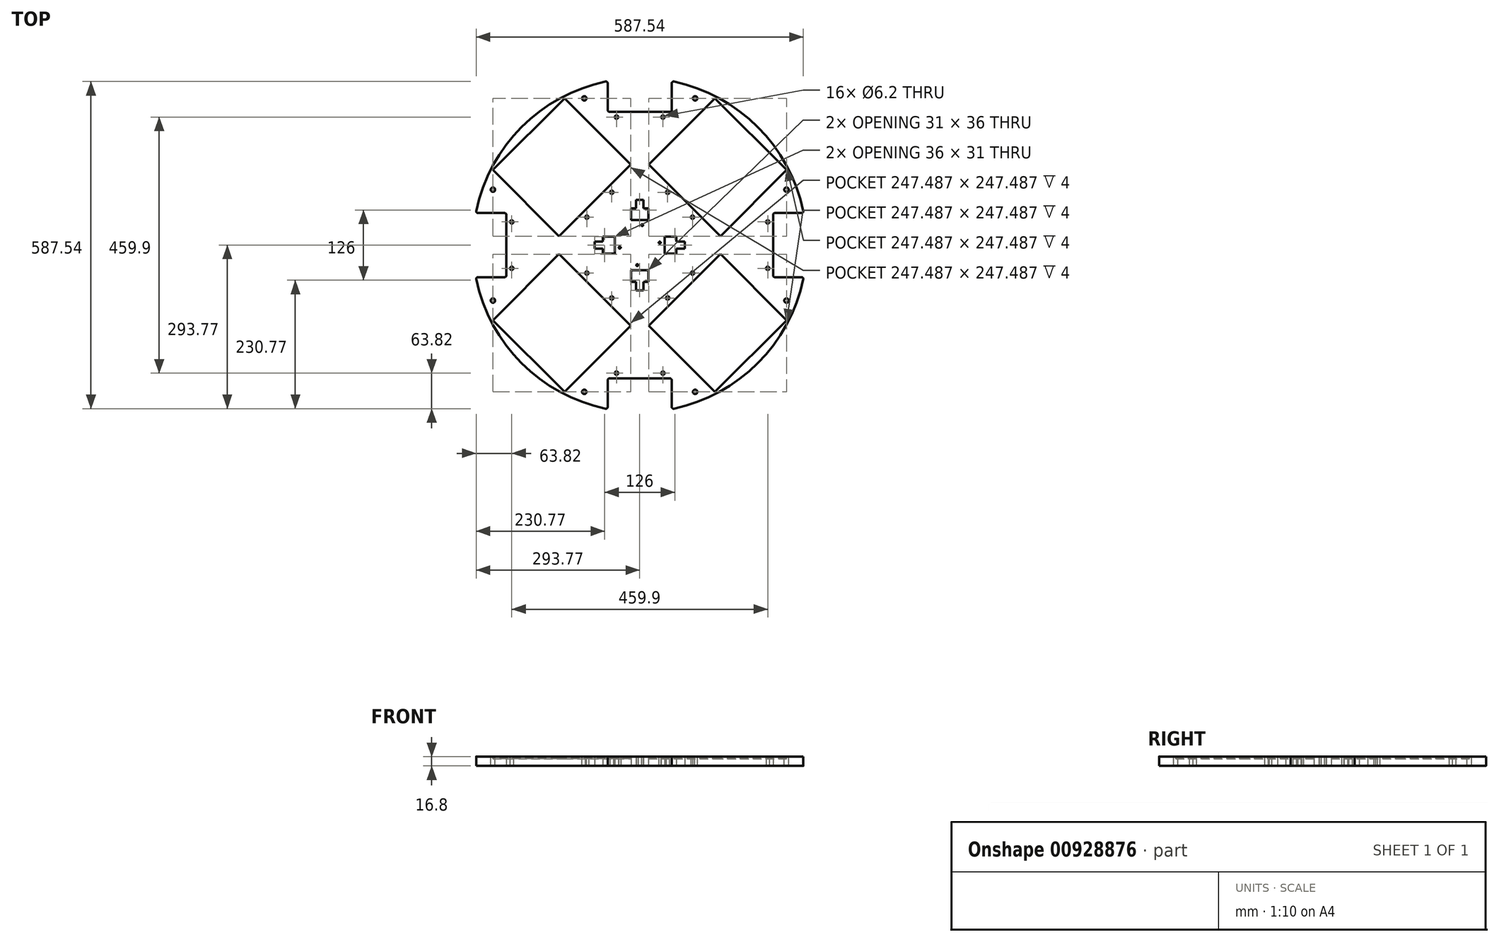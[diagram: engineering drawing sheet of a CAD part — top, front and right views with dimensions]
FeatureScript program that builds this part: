
annotation { "Feature Type Name" : "Feature", "Feature Type Description" : "" }
export const myFeature = defineFeature(function(context is Context, id is Id, definition is map)
    precondition{}
    {
        {
            var Q0;
            Q0=qCreatedBy(makeId("Top.planeOp"),FACE);
            var sketch = newSketch(context, id + "F0", { "sketchPlane" : qUnion([Q0])});
            skCircle(sketch, "E0", {"center": v(0, 0) * mm, "radius": 300 * mm});
            skLineSegment(sketch, "E1", {"start": v(300, 0) * mm, "end": v(-300, 0) * mm, "construction": true});
            skLineSegment(sketch, "E2", {"start": v(0, -300) * mm, "end": v(0, 300) * mm, "construction": true});
            skLineSegment(sketch, "E3.bottom", {"start": v(-296.52, 57.5) * mm, "end": v(-239.5, 57.5) * mm});
            skLineSegment(sketch, "E3.top", {"start": v(-296.52, -57.5) * mm, "end": v(-239.5, -57.5) * mm});
            skLineSegment(sketch, "E3.left", {"start": v(-296.52, 57.5) * mm, "end": v(-296.52, -57.5) * mm, "construction": true});
            skLineSegment(sketch, "E3.right", {"start": v(-239.5, 57.5) * mm, "end": v(-239.5, -57.5) * mm});
            skPoint(sketch, "E3.middle", {"position": v(-268, 0) * mm});
            skLineSegment(sketch, "E4.1.0", {"start": v(-57.5, -296.52) * mm, "end": v(-57.5, -239.5) * mm});
            skLineSegment(sketch, "E4.1.1", {"start": v(57.5, -296.52) * mm, "end": v(57.5, -239.5) * mm});
            skLineSegment(sketch, "E4.1.2", {"start": v(-57.5, -296.52) * mm, "end": v(57.5, -296.52) * mm});
            skLineSegment(sketch, "E4.1.3", {"start": v(-57.5, -239.5) * mm, "end": v(57.5, -239.5) * mm});
            skPoint(sketch, "E4.1.4", {"position": v(0, -268) * mm});
            skLineSegment(sketch, "E4.2.0", {"start": v(296.52, -57.5) * mm, "end": v(239.5, -57.5) * mm});
            skLineSegment(sketch, "E4.2.1", {"start": v(296.52, 57.5) * mm, "end": v(239.5, 57.5) * mm});
            skLineSegment(sketch, "E4.2.2", {"start": v(296.52, -57.5) * mm, "end": v(296.52, 57.5) * mm});
            skLineSegment(sketch, "E4.2.3", {"start": v(239.5, -57.5) * mm, "end": v(239.5, 57.5) * mm});
            skPoint(sketch, "E4.2.4", {"position": v(268, 0) * mm});
            skLineSegment(sketch, "E4.3.0", {"start": v(57.5, 296.52) * mm, "end": v(57.5, 239.5) * mm});
            skLineSegment(sketch, "E4.3.1", {"start": v(-57.5, 296.52) * mm, "end": v(-57.5, 239.5) * mm});
            skLineSegment(sketch, "E4.3.2", {"start": v(57.5, 296.52) * mm, "end": v(-57.5, 296.52) * mm});
            skLineSegment(sketch, "E4.3.3", {"start": v(57.5, 239.5) * mm, "end": v(-57.5, 239.5) * mm});
            skPoint(sketch, "E4.3.4", {"position": v(0, 268) * mm});
            skLineSegment(sketch, "E5", {"start": v(-239.5, -57.5) * mm, "end": v(-94.95, -57.5) * mm, "construction": true});
            skLineSegment(sketch, "E6", {"start": v(-229.95, -41.7) * mm, "end": v(-229.95, 0) * mm, "construction": true});
            skCircle(sketch, "E7", {"center": v(-229.95, -41.7) * mm, "radius": 3.1 * mm});
            skCircle(sketch, "E8.MirrorC", {"center": v(-229.95, 41.7) * mm, "radius": 3.1 * mm});
            skCircle(sketch, "E9.1.0", {"center": v(41.7, -229.95) * mm, "radius": 3.1 * mm});
            skCircle(sketch, "E9.1.1", {"center": v(-41.7, -229.95) * mm, "radius": 3.1 * mm});
            skCircle(sketch, "E9.2.0", {"center": v(229.95, 41.7) * mm, "radius": 3.1 * mm});
            skCircle(sketch, "E9.2.1", {"center": v(229.95, -41.7) * mm, "radius": 3.1 * mm});
            skCircle(sketch, "E9.3.0", {"center": v(-41.7, 229.95) * mm, "radius": 3.1 * mm});
            skCircle(sketch, "E9.3.1", {"center": v(41.7, 229.95) * mm, "radius": 3.1 * mm});
            skLineSegment(sketch, "E10", {"start": v(-94.95, -57.5) * mm, "end": v(-94.95, -50.2) * mm, "construction": true});
            skLineSegment(sketch, "E11", {"start": v(-94.95, -50.2) * mm, "end": v(-239.5, -50.2) * mm, "construction": true});
            skCircle(sketch, "E12", {"center": v(-94.95, -50.2) * mm, "radius": 3.1 * mm});
            skCircle(sketch, "E13.MirrorC", {"center": v(-94.95, 50.2) * mm, "radius": 3.1 * mm});
            skCircle(sketch, "E14.1.0", {"center": v(50.2, -94.95) * mm, "radius": 3.1 * mm});
            skCircle(sketch, "E14.1.1", {"center": v(-50.2, -94.95) * mm, "radius": 3.1 * mm});
            skCircle(sketch, "E14.2.0", {"center": v(94.95, 50.2) * mm, "radius": 3.1 * mm});
            skCircle(sketch, "E14.2.1", {"center": v(94.95, -50.2) * mm, "radius": 3.1 * mm});
            skCircle(sketch, "E14.3.0", {"center": v(-50.2, 94.95) * mm, "radius": 3.1 * mm});
            skCircle(sketch, "E14.3.1", {"center": v(50.2, 94.95) * mm, "radius": 3.1 * mm});
            skLineSegment(sketch, "E15", {"start": v(-294.44, 57.5) * mm, "end": v(-296.52, 57.5) * mm, "construction": true});
            skLineSegment(sketch, "E16", {"start": v(-294.44, 57.5) * mm, "end": v(-294.44, -57.5) * mm, "construction": true});
            skLineSegment(sketch, "E17", {"start": v(-296.52, -57.5) * mm, "end": v(-294.44, -57.5) * mm, "construction": true});
            skLineSegment(sketch, "E18.bottom", {"start": v(-45, -15.5) * mm, "end": v(-66, -15.5) * mm});
            skLineSegment(sketch, "E18.top", {"start": v(-45, 15.5) * mm, "end": v(-66, 15.5) * mm});
            skLineSegment(sketch, "E18.left", {"start": v(-45, -15.5) * mm, "end": v(-45, 15.5) * mm});
            skLineSegment(sketch, "E18.right", {"start": v(-66, -15.5) * mm, "end": v(-66, -6.5) * mm});
            skPoint(sketch, "E18.middle", {"position": v(-55.5, 0) * mm});
            skLineSegment(sketch, "E19", {"start": v(0, 0) * mm, "end": v(-229.45, 229.45) * mm, "construction": true});
            skLineSegment(sketch, "E20.MirrorCS", {"start": v(0, 0) * mm, "end": v(-229.45, -229.45) * mm, "construction": true});
            skLineSegment(sketch, "E21.MirrorCS", {"start": v(0, 0) * mm, "end": v(229.45, -229.45) * mm, "construction": true});
            skLineSegment(sketch, "E22", {"start": v(-66, 6.5) * mm, "end": v(-81, 6.5) * mm});
            skLineSegment(sketch, "E23", {"start": v(-81, 6.5) * mm, "end": v(-81, -6.5) * mm});
            skLineSegment(sketch, "E24", {"start": v(-81, -6.5) * mm, "end": v(-66, -6.5) * mm});
            skPoint(sketch, "E25", {"position": v(-81, 0) * mm});
            skLineSegment(sketch, "E26", {"start": v(-66, 6.5) * mm, "end": v(-66, 15.5) * mm});
            skLineSegment(sketch, "E27", {"start": v(-66, -6.5) * mm, "end": v(-66, 6.5) * mm, "construction": true});
            skLineSegment(sketch, "E28.1.0", {"start": v(-15.5, -45) * mm, "end": v(-15.5, -66) * mm});
            skPoint(sketch, "E28.1.1", {"position": v(0, -81) * mm});
            skLineSegment(sketch, "E28.1.2", {"start": v(-6.5, -66) * mm, "end": v(-6.5, -81) * mm});
            skLineSegment(sketch, "E28.1.3", {"start": v(15.5, -45) * mm, "end": v(15.5, -66) * mm});
            skLineSegment(sketch, "E28.1.4", {"start": v(15.5, -66) * mm, "end": v(6.5, -66) * mm});
            skLineSegment(sketch, "E28.1.5", {"start": v(15.5, -45) * mm, "end": v(-15.5, -45) * mm});
            skLineSegment(sketch, "E28.1.6", {"start": v(6.5, -66) * mm, "end": v(-6.5, -66) * mm, "construction": true});
            skLineSegment(sketch, "E28.1.7", {"start": v(-6.5, -81) * mm, "end": v(6.5, -81) * mm});
            skLineSegment(sketch, "E28.1.8", {"start": v(-6.5, -66) * mm, "end": v(-15.5, -66) * mm});
            skLineSegment(sketch, "E28.1.9", {"start": v(6.5, -81) * mm, "end": v(6.5, -66) * mm});
            skLineSegment(sketch, "E28.2.0", {"start": v(45, -15.5) * mm, "end": v(66, -15.5) * mm});
            skPoint(sketch, "E28.2.1", {"position": v(81, 0) * mm});
            skLineSegment(sketch, "E28.2.2", {"start": v(66, -6.5) * mm, "end": v(81, -6.5) * mm});
            skLineSegment(sketch, "E28.2.3", {"start": v(45, 15.5) * mm, "end": v(66, 15.5) * mm});
            skLineSegment(sketch, "E28.2.4", {"start": v(66, 15.5) * mm, "end": v(66, 6.5) * mm});
            skLineSegment(sketch, "E28.2.5", {"start": v(45, 15.5) * mm, "end": v(45, -15.5) * mm});
            skLineSegment(sketch, "E28.2.6", {"start": v(66, 6.5) * mm, "end": v(66, -6.5) * mm, "construction": true});
            skLineSegment(sketch, "E28.2.7", {"start": v(81, -6.5) * mm, "end": v(81, 6.5) * mm});
            skLineSegment(sketch, "E28.2.8", {"start": v(66, -6.5) * mm, "end": v(66, -15.5) * mm});
            skLineSegment(sketch, "E28.2.9", {"start": v(81, 6.5) * mm, "end": v(66, 6.5) * mm});
            skLineSegment(sketch, "E28.3.0", {"start": v(15.5, 45) * mm, "end": v(15.5, 66) * mm});
            skPoint(sketch, "E28.3.1", {"position": v(0, 81) * mm});
            skLineSegment(sketch, "E28.3.2", {"start": v(6.5, 66) * mm, "end": v(6.5, 81) * mm});
            skLineSegment(sketch, "E28.3.3", {"start": v(-15.5, 45) * mm, "end": v(-15.5, 66) * mm});
            skLineSegment(sketch, "E28.3.4", {"start": v(-15.5, 66) * mm, "end": v(-6.5, 66) * mm});
            skLineSegment(sketch, "E28.3.5", {"start": v(-15.5, 45) * mm, "end": v(15.5, 45) * mm});
            skLineSegment(sketch, "E28.3.6", {"start": v(-6.5, 66) * mm, "end": v(6.5, 66) * mm, "construction": true});
            skLineSegment(sketch, "E28.3.7", {"start": v(6.5, 81) * mm, "end": v(-6.5, 81) * mm});
            skLineSegment(sketch, "E28.3.8", {"start": v(6.5, 66) * mm, "end": v(15.5, 66) * mm});
            skLineSegment(sketch, "E28.3.9", {"start": v(-6.5, 81) * mm, "end": v(-6.5, 66) * mm});
            skLineSegment(sketch, "E29", {"start": v(-23.74, -23.74) * mm, "end": v(-46.55, -0.94) * mm, "construction": true});
            skLineSegment(sketch, "E30", {"start": v(-23.74, -23.74) * mm, "end": v(-0.94, -46.55) * mm, "construction": true});
            skLineSegment(sketch, "E31.MirrorCS", {"start": v(23.74, 23.74) * mm, "end": v(0.94, 46.55) * mm, "construction": true});
            skLineSegment(sketch, "E32.MirrorCS", {"start": v(23.74, 23.74) * mm, "end": v(46.55, 0.94) * mm, "construction": true});
            skLineSegment(sketch, "E33", {"start": v(-46.55, -0.94) * mm, "end": v(0.94, 46.55) * mm, "construction": true});
            skLineSegment(sketch, "E34", {"start": v(-0.94, -46.55) * mm, "end": v(46.55, 0.94) * mm, "construction": true});
            skCircle(sketch, "E35", {"center": v(4.47, 35.94) * mm, "radius": 1.75 * mm});
            skCircle(sketch, "E36.MirrorC", {"center": v(35.94, 4.47) * mm, "radius": 1.75 * mm});
            skCircle(sketch, "E37.MirrorC", {"center": v(-35.94, -4.47) * mm, "radius": 1.75 * mm});
            skCircle(sketch, "E38.MirrorC", {"center": v(-4.47, -35.94) * mm, "radius": 1.75 * mm});
            skLineSegment(sketch, "E39", {"start": v(-35.94, -4.47) * mm, "end": v(-4.47, -35.94) * mm, "construction": true});
            skLineSegment(sketch, "E40", {"start": v(-35.94, -4.47) * mm, "end": v(4.47, 35.94) * mm, "construction": true});
            skSolve(sketch);
        }
        {
            var Q0;
            {var subQ6=sQuery(id+"F0.wireOp",EDGE,"E3.right");Q0=makeQuery(id+"F0.imprint","IMPRINT",FACE,{"disambiguationData":[TD([[makeQuery(id+"F0.imprint","IMPRINT",EDGE,{"derivedFrom":subQ6}),1.0]])]});}
            extrude(context, id + "F1", {"entities" : qUnion([Q0]), "depth" : 16.8 * mm, "offsetDistance" : 25 * mm});
        }
        {
            var Q0;
            Q0=makeQuery(id+"F1.opExtrude","CAP_FACE",FACE,{"disambiguationData":[OSD([sQuery(id+"F0.wireOp",EDGE,"E0"),sQuery(id+"F0.wireOp",EDGE,"E3.bottom"),sQuery(id+"F0.wireOp",EDGE,"E3.top"),sQuery(id+"F0.wireOp",EDGE,"E3.left"),sQuery(id+"F0.wireOp",EDGE,"E3.right"),sQuery(id+"F0.wireOp",EDGE,"E4.1.0"),sQuery(id+"F0.wireOp",EDGE,"E4.1.1"),sQuery(id+"F0.wireOp",EDGE,"E4.1.2"),sQuery(id+"F0.wireOp",EDGE,"E4.1.3"),sQuery(id+"F0.wireOp",EDGE,"E4.2.0"),sQuery(id+"F0.wireOp",EDGE,"E4.2.1"),sQuery(id+"F0.wireOp",EDGE,"E4.2.2"),sQuery(id+"F0.wireOp",EDGE,"E4.2.3"),sQuery(id+"F0.wireOp",EDGE,"E4.3.0"),sQuery(id+"F0.wireOp",EDGE,"E4.3.1"),sQuery(id+"F0.wireOp",EDGE,"E4.3.2"),sQuery(id+"F0.wireOp",EDGE,"E4.3.3"),sQuery(id+"F0.wireOp",EDGE,"E7"),sQuery(id+"F0.wireOp",EDGE,"E8.MirrorC"),sQuery(id+"F0.wireOp",EDGE,"E9.1.0"),sQuery(id+"F0.wireOp",EDGE,"E9.1.1"),sQuery(id+"F0.wireOp",EDGE,"E9.2.0"),sQuery(id+"F0.wireOp",EDGE,"E9.2.1"),sQuery(id+"F0.wireOp",EDGE,"E9.3.0"),sQuery(id+"F0.wireOp",EDGE,"E9.3.1"),sQuery(id+"F0.wireOp",EDGE,"E12"),sQuery(id+"F0.wireOp",EDGE,"E13.MirrorC"),sQuery(id+"F0.wireOp",EDGE,"E14.1.0"),sQuery(id+"F0.wireOp",EDGE,"E14.1.1"),sQuery(id+"F0.wireOp",EDGE,"E14.2.0"),sQuery(id+"F0.wireOp",EDGE,"E14.2.1"),sQuery(id+"F0.wireOp",EDGE,"E14.3.0"),sQuery(id+"F0.wireOp",EDGE,"E14.3.1")])],"isStart":false});
            var sketch = newSketch(context, id + "F2", { "sketchPlane" : qUnion([Q0])});
            skLineSegment(sketch, "E41", {"start": v(0, 0) * mm, "end": v(-212.13, -212.13) * mm, "construction": true});
            skLineSegment(sketch, "E42", {"start": v(0, 0) * mm, "end": v(-300, 0) * mm, "construction": true});
            skLineSegment(sketch, "E43", {"start": v(-263.66, -134.96) * mm, "end": v(-134.96, -263.66) * mm});
            skLineSegment(sketch, "E44", {"start": v(-134.96, -263.66) * mm, "end": v(-16.17, -144.86) * mm});
            skLineSegment(sketch, "E45", {"start": v(-16.17, -144.86) * mm, "end": v(-144.86, -16.17) * mm});
            skLineSegment(sketch, "E46", {"start": v(-144.86, -16.17) * mm, "end": v(-263.66, -134.96) * mm});
            skPoint(sketch, "E47", {"position": v(-199.3, -199.3) * mm});
            skLineSegment(sketch, "E48", {"start": v(0, 0) * mm, "end": v(212.13, 212.13) * mm, "construction": true});
            skLineSegment(sketch, "E49", {"start": v(0, 0) * mm, "end": v(212.13, -212.13) * mm, "construction": true});
            skLineSegment(sketch, "E50", {"start": v(-263.66, -134.96) * mm, "end": v(-266.48, -137.8) * mm});
            skLineSegment(sketch, "E51.1.0", {"start": v(16.17, -144.86) * mm, "end": v(134.96, -263.66) * mm});
            skLineSegment(sketch, "E51.1.1", {"start": v(144.86, -16.17) * mm, "end": v(16.17, -144.86) * mm});
            skLineSegment(sketch, "E51.1.2", {"start": v(263.66, -134.96) * mm, "end": v(144.86, -16.17) * mm});
            skLineSegment(sketch, "E51.1.3", {"start": v(134.96, -263.66) * mm, "end": v(263.66, -134.96) * mm});
            skLineSegment(sketch, "E51.2.0", {"start": v(144.86, 16.17) * mm, "end": v(263.66, 134.96) * mm});
            skLineSegment(sketch, "E51.2.1", {"start": v(16.17, 144.86) * mm, "end": v(144.86, 16.17) * mm});
            skLineSegment(sketch, "E51.2.2", {"start": v(134.96, 263.66) * mm, "end": v(16.17, 144.86) * mm});
            skLineSegment(sketch, "E51.2.3", {"start": v(263.66, 134.96) * mm, "end": v(134.96, 263.66) * mm});
            skLineSegment(sketch, "E51.3.0", {"start": v(-16.17, 144.86) * mm, "end": v(-134.96, 263.66) * mm});
            skLineSegment(sketch, "E51.3.1", {"start": v(-144.86, 16.17) * mm, "end": v(-16.17, 144.86) * mm});
            skLineSegment(sketch, "E51.3.2", {"start": v(-263.66, 134.96) * mm, "end": v(-144.86, 16.17) * mm});
            skLineSegment(sketch, "E51.3.3", {"start": v(-134.96, 263.66) * mm, "end": v(-263.66, 134.96) * mm});
            skPoint(sketch, "E51.center", {"position": v(0, 0) * mm});
            skSolve(sketch);
        }
        {
            var Q0;
            Q0=qSketchRegion(id+"F2",true);
            extrude(context, id + "F3", {"entities" : qUnion([Q0]), "operationType" : NewBodyOperationType.REMOVE, "oppositeDirection" : true, "depth" : 4 * mm, "offsetDistance" : 25 * mm});
        }
        {
            var Q0;
            Q0=makeQuery(id+"F1.opExtrude","CAP_FACE",FACE,{"disambiguationData":[OSD([sQuery(id+"F0.wireOp",EDGE,"E0"),sQuery(id+"F0.wireOp",EDGE,"E3.bottom"),sQuery(id+"F0.wireOp",EDGE,"E3.top"),sQuery(id+"F0.wireOp",EDGE,"E3.left"),sQuery(id+"F0.wireOp",EDGE,"E3.right"),sQuery(id+"F0.wireOp",EDGE,"E4.1.0"),sQuery(id+"F0.wireOp",EDGE,"E4.1.1"),sQuery(id+"F0.wireOp",EDGE,"E4.1.2"),sQuery(id+"F0.wireOp",EDGE,"E4.1.3"),sQuery(id+"F0.wireOp",EDGE,"E4.2.0"),sQuery(id+"F0.wireOp",EDGE,"E4.2.1"),sQuery(id+"F0.wireOp",EDGE,"E4.2.2"),sQuery(id+"F0.wireOp",EDGE,"E4.2.3"),sQuery(id+"F0.wireOp",EDGE,"E4.3.0"),sQuery(id+"F0.wireOp",EDGE,"E4.3.1"),sQuery(id+"F0.wireOp",EDGE,"E4.3.2"),sQuery(id+"F0.wireOp",EDGE,"E4.3.3"),sQuery(id+"F0.wireOp",EDGE,"E7"),sQuery(id+"F0.wireOp",EDGE,"E8.MirrorC"),sQuery(id+"F0.wireOp",EDGE,"E9.1.0"),sQuery(id+"F0.wireOp",EDGE,"E9.1.1"),sQuery(id+"F0.wireOp",EDGE,"E9.2.0"),sQuery(id+"F0.wireOp",EDGE,"E9.2.1"),sQuery(id+"F0.wireOp",EDGE,"E9.3.0"),sQuery(id+"F0.wireOp",EDGE,"E9.3.1"),sQuery(id+"F0.wireOp",EDGE,"E12"),sQuery(id+"F0.wireOp",EDGE,"E13.MirrorC"),sQuery(id+"F0.wireOp",EDGE,"E14.1.0"),sQuery(id+"F0.wireOp",EDGE,"E14.1.1"),sQuery(id+"F0.wireOp",EDGE,"E14.2.0"),sQuery(id+"F0.wireOp",EDGE,"E14.2.1"),sQuery(id+"F0.wireOp",EDGE,"E14.3.0"),sQuery(id+"F0.wireOp",EDGE,"E14.3.1"),sQuery(id+"F0.wireOp",EDGE,"E18.bottom"),sQuery(id+"F0.wireOp",EDGE,"E18.top"),sQuery(id+"F0.wireOp",EDGE,"E18.left"),sQuery(id+"F0.wireOp",EDGE,"E18.right"),sQuery(id+"F0.wireOp",EDGE,"vhIM6kYj-bil8-T5aC-Hw9W-HzG7wACOchpu.bottom"),sQuery(id+"F0.wireOp",EDGE,"vhIM6kYj-bil8-T5aC-Hw9W-HzG7wACOchpu.top"),sQuery(id+"F0.wireOp",EDGE,"vhIM6kYj-bil8-T5aC-Hw9W-HzG7wACOchpu.left"),sQuery(id+"F0.wireOp",EDGE,"vhIM6kYj-bil8-T5aC-Hw9W-HzG7wACOchpu.right"),sQuery(id+"F0.wireOp",EDGE,"e5db2dc1-b70e-487e-85e1-c1db5f647828.1.0"),sQuery(id+"F0.wireOp",EDGE,"e5db2dc1-b70e-487e-85e1-c1db5f647828.1.1"),sQuery(id+"F0.wireOp",EDGE,"e5db2dc1-b70e-487e-85e1-c1db5f647828.1.2"),sQuery(id+"F0.wireOp",EDGE,"e5db2dc1-b70e-487e-85e1-c1db5f647828.1.3"),sQuery(id+"F0.wireOp",EDGE,"e5db2dc1-b70e-487e-85e1-c1db5f647828.1.4"),sQuery(id+"F0.wireOp",EDGE,"e5db2dc1-b70e-487e-85e1-c1db5f647828.1.5"),sQuery(id+"F0.wireOp",EDGE,"e5db2dc1-b70e-487e-85e1-c1db5f647828.1.6"),sQuery(id+"F0.wireOp",EDGE,"e5db2dc1-b70e-487e-85e1-c1db5f647828.1.7"),sQuery(id+"F0.wireOp",EDGE,"e5db2dc1-b70e-487e-85e1-c1db5f647828.2.0"),sQuery(id+"F0.wireOp",EDGE,"e5db2dc1-b70e-487e-85e1-c1db5f647828.2.1"),sQuery(id+"F0.wireOp",EDGE,"e5db2dc1-b70e-487e-85e1-c1db5f647828.2.2"),sQuery(id+"F0.wireOp",EDGE,"e5db2dc1-b70e-487e-85e1-c1db5f647828.2.3"),sQuery(id+"F0.wireOp",EDGE,"e5db2dc1-b70e-487e-85e1-c1db5f647828.2.4"),sQuery(id+"F0.wireOp",EDGE,"e5db2dc1-b70e-487e-85e1-c1db5f647828.2.5"),sQuery(id+"F0.wireOp",EDGE,"e5db2dc1-b70e-487e-85e1-c1db5f647828.2.6"),sQuery(id+"F0.wireOp",EDGE,"e5db2dc1-b70e-487e-85e1-c1db5f647828.2.7"),sQuery(id+"F0.wireOp",EDGE,"e5db2dc1-b70e-487e-85e1-c1db5f647828.3.0"),sQuery(id+"F0.wireOp",EDGE,"e5db2dc1-b70e-487e-85e1-c1db5f647828.3.1"),sQuery(id+"F0.wireOp",EDGE,"e5db2dc1-b70e-487e-85e1-c1db5f647828.3.2"),sQuery(id+"F0.wireOp",EDGE,"e5db2dc1-b70e-487e-85e1-c1db5f647828.3.3"),sQuery(id+"F0.wireOp",EDGE,"e5db2dc1-b70e-487e-85e1-c1db5f647828.3.4"),sQuery(id+"F0.wireOp",EDGE,"e5db2dc1-b70e-487e-85e1-c1db5f647828.3.5"),sQuery(id+"F0.wireOp",EDGE,"e5db2dc1-b70e-487e-85e1-c1db5f647828.3.6"),sQuery(id+"F0.wireOp",EDGE,"e5db2dc1-b70e-487e-85e1-c1db5f647828.3.7")])],"isStart":false});
            var sketch = newSketch(context, id + "F4", { "sketchPlane" : qUnion([Q0])});
            skLineSegment(sketch, "E52", {"start": v(-263.66, -99.6) * mm, "end": v(-245.98, -117.28) * mm, "construction": true});
            skCircle(sketch, "E53", {"center": v(-263.66, -99.6) * mm, "radius": 4 * mm});
            skLineSegment(sketch, "E54", {"start": v(-99.6, -263.66) * mm, "end": v(-117.28, -245.98) * mm, "construction": true});
            skCircle(sketch, "E55", {"center": v(-99.6, -263.66) * mm, "radius": 4 * mm});
            skCircle(sketch, "E56.1.0", {"center": v(99.6, -263.66) * mm, "radius": 4 * mm});
            skCircle(sketch, "E56.1.1", {"center": v(263.66, -99.6) * mm, "radius": 4 * mm});
            skCircle(sketch, "E56.2.0", {"center": v(263.66, 99.6) * mm, "radius": 4 * mm});
            skCircle(sketch, "E56.2.1", {"center": v(99.6, 263.66) * mm, "radius": 4 * mm});
            skCircle(sketch, "E56.3.0", {"center": v(-99.6, 263.66) * mm, "radius": 4 * mm});
            skCircle(sketch, "E56.3.1", {"center": v(-263.66, 99.6) * mm, "radius": 4 * mm});
            skPoint(sketch, "E56.center", {"position": v(0, 0) * mm});
            skSolve(sketch);
        }
        {
            var Q0;
            Q0=qSketchRegion(id+"F4",true);
            extrude(context, id + "F5", {"entities" : qUnion([Q0]), "operationType" : NewBodyOperationType.REMOVE, "oppositeDirection" : true, "depth" : 25 * mm, "offsetDistance" : 25 * mm});
        }
        {
            var Q0;
            Q0=makeQuery(id+"F1.opExtrude","SWEPT_EDGE",EDGE,{"disambiguationData":[OSD([sQuery(id+"F0.wireOp",EDGE,"E4.1.1"),sQuery(id+"F0.wireOp",EDGE,"E4.1.3")])]});
            var Q1;
            Q1=makeQuery(id+"F1.opExtrude","SWEPT_EDGE",EDGE,{"disambiguationData":[OSD([sQuery(id+"F0.wireOp",EDGE,"E0"),sQuery(id+"F0.wireOp",EDGE,"E4.1.1")])]});
            var Q2;
            Q2=makeQuery(id+"F1.opExtrude","SWEPT_EDGE",EDGE,{"disambiguationData":[OSD([sQuery(id+"F0.wireOp",EDGE,"E4.1.0"),sQuery(id+"F0.wireOp",EDGE,"E4.1.3")])]});
            var Q3;
            Q3=makeQuery(id+"F1.opExtrude","SWEPT_EDGE",EDGE,{"disambiguationData":[OSD([sQuery(id+"F0.wireOp",EDGE,"E0"),sQuery(id+"F0.wireOp",EDGE,"E4.1.0")])]});
            var Q4;
            Q4=makeQuery(id+"F1.opExtrude","SWEPT_EDGE",EDGE,{"disambiguationData":[OSD([sQuery(id+"F0.wireOp",EDGE,"E0"),sQuery(id+"F0.wireOp",EDGE,"E3.bottom")])]});
            var Q5;
            Q5=makeQuery(id+"F1.opExtrude","SWEPT_EDGE",EDGE,{"disambiguationData":[OSD([sQuery(id+"F0.wireOp",EDGE,"E3.bottom"),sQuery(id+"F0.wireOp",EDGE,"E3.right")])]});
            var Q6;
            Q6=makeQuery(id+"F1.opExtrude","SWEPT_EDGE",EDGE,{"disambiguationData":[OSD([sQuery(id+"F0.wireOp",EDGE,"E3.top"),sQuery(id+"F0.wireOp",EDGE,"E3.right")])]});
            var Q7;
            Q7=makeQuery(id+"F1.opExtrude","SWEPT_EDGE",EDGE,{"disambiguationData":[OSD([sQuery(id+"F0.wireOp",EDGE,"E0"),sQuery(id+"F0.wireOp",EDGE,"E3.top")])]});
            var Q8;
            Q8=makeQuery(id+"F1.opExtrude","SWEPT_EDGE",EDGE,{"disambiguationData":[OSD([sQuery(id+"F0.wireOp",EDGE,"E4.3.0"),sQuery(id+"F0.wireOp",EDGE,"E4.3.3")])]});
            var Q9;
            Q9=makeQuery(id+"F1.opExtrude","SWEPT_EDGE",EDGE,{"disambiguationData":[OSD([sQuery(id+"F0.wireOp",EDGE,"E0"),sQuery(id+"F0.wireOp",EDGE,"E4.2.0")])]});
            var Q10;
            Q10=makeQuery(id+"F1.opExtrude","SWEPT_EDGE",EDGE,{"disambiguationData":[OSD([sQuery(id+"F0.wireOp",EDGE,"E0"),sQuery(id+"F0.wireOp",EDGE,"E4.3.0")])]});
            var Q11;
            Q11=makeQuery(id+"F1.opExtrude","SWEPT_EDGE",EDGE,{"disambiguationData":[OSD([sQuery(id+"F0.wireOp",EDGE,"E4.3.1"),sQuery(id+"F0.wireOp",EDGE,"E4.3.3")])]});
            var Q12;
            Q12=makeQuery(id+"F1.opExtrude","SWEPT_EDGE",EDGE,{"disambiguationData":[OSD([sQuery(id+"F0.wireOp",EDGE,"E0"),sQuery(id+"F0.wireOp",EDGE,"E4.3.1")])]});
            var Q13;
            Q13=makeQuery(id+"F1.opExtrude","SWEPT_EDGE",EDGE,{"disambiguationData":[OSD([sQuery(id+"F0.wireOp",EDGE,"E4.2.0"),sQuery(id+"F0.wireOp",EDGE,"E4.2.3")])]});
            var Q14;
            Q14=makeQuery(id+"F1.opExtrude","SWEPT_EDGE",EDGE,{"disambiguationData":[OSD([sQuery(id+"F0.wireOp",EDGE,"E4.2.1"),sQuery(id+"F0.wireOp",EDGE,"E4.2.3")])]});
            var Q15;
            Q15=makeQuery(id+"F1.opExtrude","SWEPT_EDGE",EDGE,{"disambiguationData":[OSD([sQuery(id+"F0.wireOp",EDGE,"E0"),sQuery(id+"F0.wireOp",EDGE,"E4.2.1")])]});
            fillet(context, id + "F6", {"entities" : qUnion([Q0, Q1, Q2, Q3, Q4, Q5, Q6, Q7, Q8, Q9, Q10, Q11, Q12, Q13, Q14, Q15]), "radius" : 3 * mm, "tangentPropagation" : true, "allowEdgeOverflow" : false});
        }
    });
